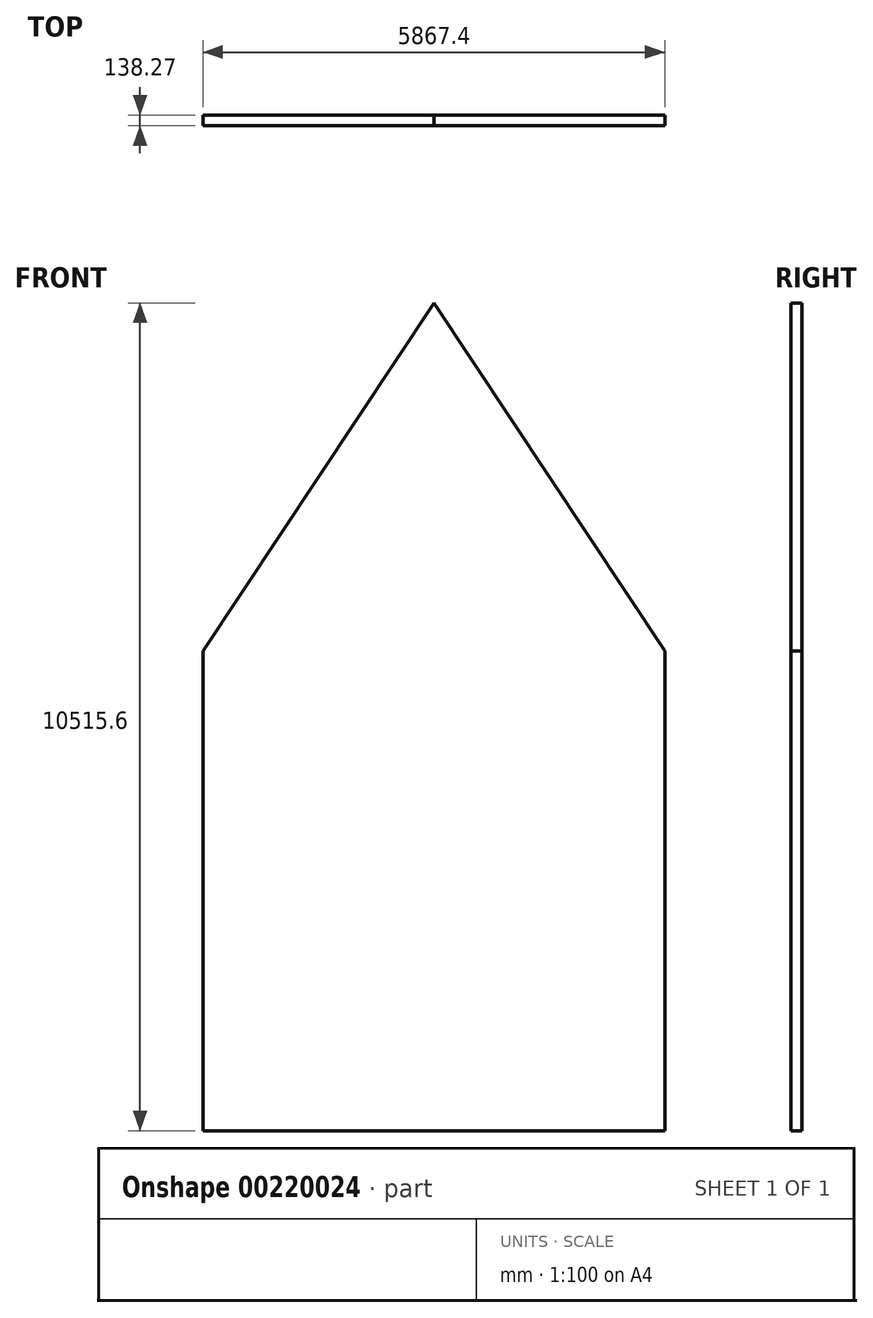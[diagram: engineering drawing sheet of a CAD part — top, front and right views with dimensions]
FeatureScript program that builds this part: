
annotation { "Feature Type Name" : "Feature", "Feature Type Description" : "" }
export const myFeature = defineFeature(function(context is Context, id is Id, definition is map)
    precondition{}
    {
        {
            var Q0;
            Q0=qCreatedBy(makeId("Front.planeOp"),FACE);
            var sketch = newSketch(context, id + "F0", { "sketchPlane" : qUnion([Q0])});
            skLineSegment(sketch, "E0", {"start": v(0, 0) * mm, "end": v(5867.4, 0) * mm});
            skLineSegment(sketch, "E1", {"start": v(5867.4, 0) * mm, "end": v(5867.4, 6096) * mm});
            skLineSegment(sketch, "E2", {"start": v(5867.4, 6096) * mm, "end": v(2933.7, 10515.6) * mm});
            skLineSegment(sketch, "E3", {"start": v(2933.7, 10515.6) * mm, "end": v(0, 6096) * mm});
            skLineSegment(sketch, "E4", {"start": v(0, 6096) * mm, "end": v(0, 0) * mm});
            skSolve(sketch);
        }
        {
            var Q0;
            Q0=makeQuery(id+"F0.imprint","IMPRINT",FACE,{"disambiguationData":[TD([[makeQuery(id+"F0.imprint","IMPRINT",EDGE,{"derivedFrom":sQuery(id+"F0.wireOp",EDGE,"E0")}),1.0]])]});
            extrude(context, id + "F1", {"entities" : qUnion([Q0]), "depth" : 138.27 * mm});
        }
    });
